# Revit family: MV-HEP
name_source: partatom
category: Mechanical Equipment
revit_build: Autodesk Revit 2016 (Build: 20150714_1515(x64)
units: mm (PartAtom-declared; Revit-internal decimal feet)

## family parameters
Always vertical = Yes
Cut with Voids When Loaded = No
OmniClass Number = 23.75.00.00
OmniClass Title = Climate Control (HVAC)
Part Type = Normal
Room Calculation Point = No
Round Connector Dimension = Use Radius
Shared = No
Work Plane-Based = No

## types (65) — shared parameters
Manufacturer = Anemostat
Model = MV-HEP
URL = http://www.anemostat.com

## per-type parameters (varying)
| type | Diff Length | Diff Width | Duct Radius | Duct Size | Inlet Radius | Inlet Size | Module Length | Module Width | Plenum Length |
| MV-HEP - 12x48, 06" Round Inlet | 47 3/4" | 11 3/4" | 3" | 6" | 3" | 6" | 48" | 12" | 45 5/16" |
| MV-HEP - 12x48, 07" Round Inlet | 47 3/4" | 11 3/4" | 4" | 7" | 3" | 7" | 48" | 12" | 45 5/16" |
| MV-HEP - 12x48, 08" Round Inlet | 47 3/4" | 11 3/4" | 4" | 8" | 4" | 8" | 48" | 12" | 45 5/16" |
| MV-HEP - 12x48, 05" Round Inlet | 47 3/4" | 11 3/4" | 3" | 5" | 2" | 5" | 48" | 12" | 45 5/16" |
| MV-HEP - 24x24, 05" Round Inlet | 23 3/4" | 23 3/4" | 3" | 5" | 2" | 5" | 24" | 24" | 21 5/16" |
| MV-HEP - 24x24, 06" Round Inlet | 23 3/4" | 23 3/4" | 3" | 6" | 3" | 6" | 24" | 24" | 21 5/16" |
| MV-HEP - 24x24, 07" Round Inlet | 23 3/4" | 23 3/4" | 4" | 7" | 3" | 7" | 24" | 24" | 21 5/16" |
| MV-HEP - 24x24, 08" Round Inlet | 23 3/4" | 23 3/4" | 4" | 8" | 4" | 8" | 24" | 24" | 21 5/16" |
| MV-HEP - 24x48, 05" Round Inlet | 47 3/4" | 23 3/4" | 3" | 5" | 2" | 5" | 48" | 24" | 37 5/16" |
| MV-HEP - 24x48, 06" Round Inlet | 47 3/4" | 23 3/4" | 3" | 6" | 3" | 6" | 48" | 24" | 37 5/16" |
| MV-HEP - 24x48, 07" Round Inlet | 47 3/4" | 23 3/4" | 4" | 7" | 3" | 7" | 48" | 24" | 37 5/16" |
| MV-HEP - 24x48, 08" Round Inlet | 47 3/4" | 23 3/4" | 4" | 8" | 4" | 8" | 48" | 24" | 37 5/16" |
| MV-HEP - 24x24, 09" Round Inlet | 23 3/4" | 23 3/4" | 5" | 9" | 4" | 9" | 24" | 24" | 21 5/16" |
| MV-HEP - 24x24, 10" Round Inlet | 23 3/4" | 23 3/4" | 5" | 10" | 5" | 10" | 24" | 24" | 21 5/16" |
| MV-HEP - 24x24, 12" Round Inlet | 23 3/4" | 23 3/4" | 6" | 12" | 6" | 12" | 24" | 24" | 21 5/16" |
| MV-HEP - 24x24, 14" Round Inlet | 23 3/4" | 23 3/4" | 7" | 14" | 7" | 14" | 24" | 24" | 21 5/16" |
| MV-HEP - 24x24, 16" Round Inlet | 23 3/4" | 23 3/4" | 8" | 16" | 8" | 16" | 24" | 24" | 21 5/16" |
| MV-HEP - 24x36, 05" Round Inlet | 35 3/4" | 23 3/4" | 3" | 5" | 2" | 5" | 36" | 24" | 21 5/16" |
| MV-HEP - 24x36, 06" Round Inlet | 35 3/4" | 23 3/4" | 3" | 6" | 3" | 6" | 36" | 24" | 21 5/16" |
| MV-HEP - 24x36, 07" Round Inlet | 35 3/4" | 23 3/4" | 4" | 7" | 3" | 7" | 36" | 24" | 21 5/16" |
| MV-HEP - 24x36, 08" Round Inlet | 35 3/4" | 23 3/4" | 4" | 8" | 4" | 8" | 36" | 24" | 21 5/16" |
| MV-HEP - 24x36, 09" Round Inlet | 35 3/4" | 23 3/4" | 5" | 9" | 4" | 9" | 36" | 24" | 21 5/16" |
| MV-HEP - 24x36, 10" Round Inlet | 35 3/4" | 23 3/4" | 5" | 10" | 5" | 10" | 36" | 24" | 21 5/16" |
| MV-HEP - 24x36, 12" Round Inlet | 35 3/4" | 23 3/4" | 6" | 12" | 6" | 12" | 36" | 24" | 21 5/16" |
| MV-HEP - 24x36, 14" Round Inlet | 35 3/4" | 23 3/4" | 7" | 14" | 7" | 14" | 36" | 24" | 21 5/16" |
| MV-HEP - 24x36, 16" Round Inlet | 35 3/4" | 23 3/4" | 8" | 16" | 8" | 16" | 36" | 24" | 21 5/16" |
| MV-HEP - 24x48, 09" Round Inlet | 47 3/4" | 23 3/4" | 5" | 9" | 4" | 9" | 48" | 24" | 37 5/16" |
| MV-HEP - 24x48, 10" Round Inlet | 47 3/4" | 23 3/4" | 5" | 10" | 5" | 10" | 48" | 24" | 37 5/16" |
| MV-HEP - 24x48, 12" Round Inlet | 47 3/4" | 23 3/4" | 6" | 12" | 6" | 12" | 48" | 24" | 37 5/16" |
| MV-HEP - 24x48, 14" Round Inlet | 47 3/4" | 23 3/4" | 7" | 14" | 7" | 14" | 48" | 24" | 37 5/16" |
| MV-HEP - 24x48, 16" Round Inlet | 47 3/4" | 23 3/4" | 8" | 16" | 8" | 16" | 48" | 24" | 37 5/16" |
| MV-HEP - 12x24, 05" Round Inlet | 23 3/4" | 11 3/4" | 3" | 5" | 2" | 5" | 24" | 12" | 21 5/16" |
| MV-HEP - 12x24, 06" Round Inlet | 23 3/4" | 11 3/4" | 3" | 6" | 3" | 6" | 24" | 12" | 21 5/16" |
| MV-HEP - 12x24, 07" Round Inlet | 23 3/4" | 11 3/4" | 4" | 7" | 3" | 7" | 24" | 12" | 21 5/16" |
| MV-HEP - 12x24, 08" Round Inlet | 23 3/4" | 11 3/4" | 4" | 8" | 4" | 8" | 24" | 12" | 21 5/16" |
| MV-HEP - 12x36, 05" Round Inlet | 35 3/4" | 11 3/4" | 3" | 5" | 2" | 5" | 36" | 12" | 33 5/16" |
| MV-HEP - 12x36, 06" Round Inlet | 35 3/4" | 11 3/4" | 3" | 6" | 3" | 6" | 36" | 12" | 33 5/16" |
| MV-HEP - 12x36, 07" Round Inlet | 35 3/4" | 11 3/4" | 4" | 7" | 3" | 7" | 36" | 12" | 33 5/16" |
| MV-HEP - 12x36, 08" Round Inlet | 35 3/4" | 11 3/4" | 4" | 8" | 4" | 8" | 36" | 12" | 33 5/16" |
| MV-HEP - 12x60, 05" Round Inlet | 59 3/4" | 11 3/4" | 3" | 5" | 2" | 5" | 60" | 12" | 49 7/32" |
| MV-HEP - 12x60, 06" Round Inlet | 59 3/4" | 11 3/4" | 3" | 6" | 3" | 6" | 60" | 12" | 49 7/32" |
| MV-HEP - 12x60, 07" Round Inlet | 59 3/4" | 11 3/4" | 4" | 7" | 3" | 7" | 60" | 12" | 49 7/32" |
| MV-HEP - 12x60, 08" Round Inlet | 59 3/4" | 11 3/4" | 4" | 8" | 4" | 8" | 60" | 12" | 49 7/32" |
| MV-HEP - 12x72, 05" Round Inlet | 71 3/4" | 11 3/4" | 3" | 5" | 2" | 5" | 72" | 12" | 61 7/32" |
| MV-HEP - 12x72, 06" Round Inlet | 71 3/4" | 11 3/4" | 3" | 6" | 3" | 6" | 72" | 12" | 61 7/32" |
| MV-HEP - 12x72, 07" Round Inlet | 71 3/4" | 11 3/4" | 4" | 7" | 3" | 7" | 72" | 12" | 61 7/32" |
| MV-HEP - 12x72, 08" Round Inlet | 71 3/4" | 11 3/4" | 4" | 8" | 4" | 8" | 72" | 12" | 61 7/32" |
| MV-HEP - 24x60, 05" Round Inlet | 59 3/4" | 23 3/4" | 3" | 5" | 2" | 5" | 60" | 24" | 37 5/16" |
| MV-HEP - 24x60, 06" Round Inlet | 59 3/4" | 23 3/4" | 3" | 6" | 3" | 6" | 60" | 24" | 37 5/16" |
| MV-HEP - 24x60, 07" Round Inlet | 59 3/4" | 23 3/4" | 4" | 7" | 3" | 7" | 60" | 24" | 37 5/16" |
| MV-HEP - 24x60, 08" Round Inlet | 59 3/4" | 23 3/4" | 4" | 8" | 4" | 8" | 60" | 24" | 37 5/16" |
| MV-HEP - 24x60, 09" Round Inlet | 59 3/4" | 23 3/4" | 5" | 9" | 4" | 9" | 60" | 24" | 37 5/16" |
| MV-HEP - 24x60, 10" Round Inlet | 59 3/4" | 23 3/4" | 5" | 10" | 5" | 10" | 60" | 24" | 37 5/16" |
| MV-HEP - 24x60, 12" Round Inlet | 59 3/4" | 23 3/4" | 6" | 12" | 6" | 12" | 60" | 24" | 37 5/16" |
| MV-HEP - 24x60, 14" Round Inlet | 59 3/4" | 23 3/4" | 7" | 14" | 7" | 14" | 60" | 24" | 37 5/16" |
| MV-HEP - 24x60, 16" Round Inlet | 59 3/4" | 23 3/4" | 8" | 16" | 8" | 16" | 60" | 24" | 37 5/16" |
| MV-HEP - 24x72, 05" Round Inlet | 71 3/4" | 23 3/4" | 3" | 5" | 2" | 5" | 72" | 24" | 37 5/16" |
| MV-HEP - 24x72, 06" Round Inlet | 71 3/4" | 23 3/4" | 3" | 6" | 3" | 6" | 72" | 24" | 37 5/16" |
| MV-HEP - 24x72, 07" Round Inlet | 71 3/4" | 23 3/4" | 4" | 7" | 3" | 7" | 72" | 24" | 37 5/16" |
| MV-HEP - 24x72, 08" Round Inlet | 71 3/4" | 23 3/4" | 4" | 8" | 4" | 8" | 72" | 24" | 37 5/16" |
| MV-HEP - 24x72, 09" Round Inlet | 71 3/4" | 23 3/4" | 5" | 9" | 4" | 9" | 72" | 24" | 37 5/16" |
| MV-HEP - 24x72, 10" Round Inlet | 71 3/4" | 23 3/4" | 5" | 10" | 5" | 10" | 72" | 24" | 37 5/16" |
| MV-HEP - 24x72, 12" Round Inlet | 71 3/4" | 23 3/4" | 6" | 12" | 6" | 12" | 72" | 24" | 37 5/16" |
| MV-HEP - 24x72, 14" Round Inlet | 71 3/4" | 23 3/4" | 7" | 14" | 7" | 14" | 72" | 24" | 37 5/16" |
| MV-HEP - 24x72, 16" Round Inlet | 71 3/4" | 23 3/4" | 8" | 16" | 8" | 16" | 72" | 24" | 37 5/16" |

## geometry (parser evidence)
native form markers: Sweep x3
no freeform markers — native parametric forms only
